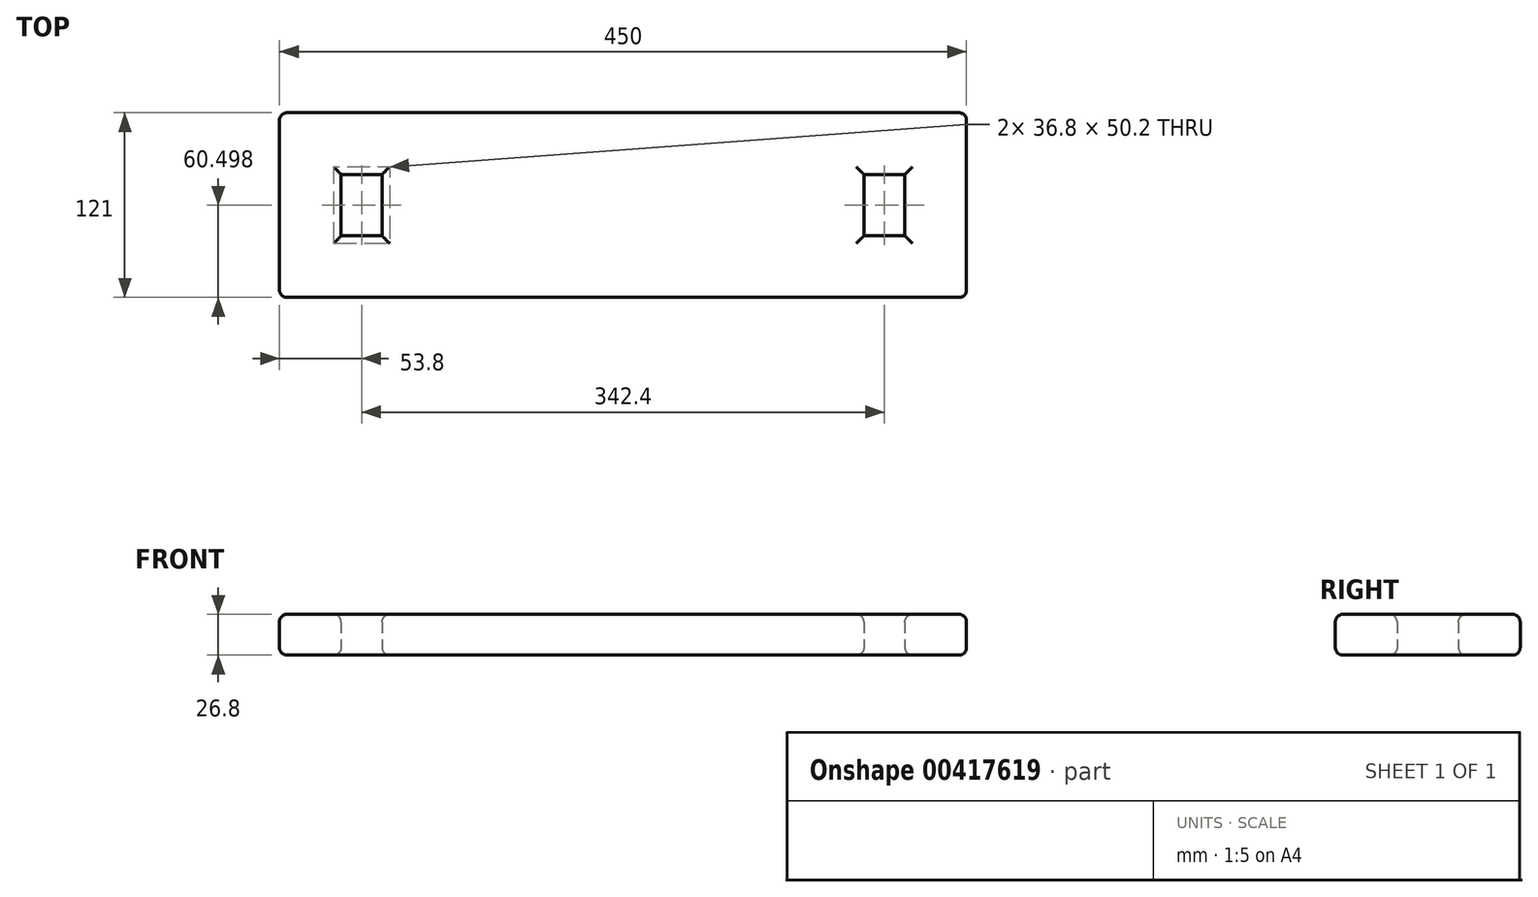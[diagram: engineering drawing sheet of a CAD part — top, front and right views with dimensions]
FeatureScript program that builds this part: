
annotation { "Feature Type Name" : "Feature", "Feature Type Description" : "" }
export const myFeature = defineFeature(function(context is Context, id is Id, definition is map)
    precondition{}
    {
        {
            var Q0;
            Q0=qCreatedBy(makeId("Top.planeOp"),FACE);
            var sketch = newSketch(context, id + "F0", { "sketchPlane" : qUnion([Q0])});
            skLineSegment(sketch, "E0.bottom", {"start": v(-382.8, 117.82) * mm, "end": v(67.2, 117.82) * mm});
            skLineSegment(sketch, "E0.top", {"start": v(-382.8, -3.18) * mm, "end": v(67.2, -3.18) * mm});
            skLineSegment(sketch, "E0.left", {"start": v(-382.8, 117.82) * mm, "end": v(-382.8, -3.18) * mm});
            skLineSegment(sketch, "E0.right", {"start": v(67.2, 117.82) * mm, "end": v(67.2, -3.18) * mm});
            skLineSegment(sketch, "E1.bottom", {"start": v(-342.4, 77.42) * mm, "end": v(-315.6, 77.42) * mm});
            skLineSegment(sketch, "E1.top", {"start": v(-342.4, 37.22) * mm, "end": v(-315.6, 37.22) * mm});
            skLineSegment(sketch, "E1.left", {"start": v(-342.4, 77.42) * mm, "end": v(-342.4, 37.22) * mm});
            skLineSegment(sketch, "E1.right", {"start": v(-315.6, 77.42) * mm, "end": v(-315.6, 37.22) * mm});
            skLineSegment(sketch, "E2.bottom", {"start": v(26.8, 77.42) * mm, "end": v(0, 77.42) * mm});
            skLineSegment(sketch, "E2.top", {"start": v(26.8, 37.22) * mm, "end": v(0, 37.22) * mm});
            skLineSegment(sketch, "E2.left", {"start": v(26.8, 77.42) * mm, "end": v(26.8, 37.22) * mm});
            skLineSegment(sketch, "E2.right", {"start": v(0, 77.42) * mm, "end": v(0, 37.22) * mm});
            skPoint(sketch, "E3.right.end.orphan", {"position": v(-342.4, 37.22) * mm});
            skPoint(sketch, "E4.right.end.orphan", {"position": v(26.8, 37.22) * mm});
            skSolve(sketch);
        }
        {
            var Q0;
            Q0=makeQuery(id+"F0.imprint","IMPRINT",FACE,{"disambiguationData":[TD([[makeQuery(id+"F0.imprint","IMPRINT",EDGE,{"derivedFrom":sQuery(id+"F0.wireOp",EDGE,"E0.bottom")}),-1.0]])]});
            extrude(context, id + "F1", {"entities" : qUnion([Q0]), "depth" : 26.8 * mm});
        }
        {
            var Q0;
            Q0=makeQuery(id+"F1.opExtrude","CAP_FACE",FACE,{"disambiguationData":[OSD([sQuery(id+"F0.wireOp",EDGE,"E0.bottom"),sQuery(id+"F0.wireOp",EDGE,"E0.top"),sQuery(id+"F0.wireOp",EDGE,"E0.left"),sQuery(id+"F0.wireOp",EDGE,"E0.right"),sQuery(id+"F0.wireOp",EDGE,"E1.bottom"),sQuery(id+"F0.wireOp",EDGE,"E1.top"),sQuery(id+"F0.wireOp",EDGE,"E1.left"),sQuery(id+"F0.wireOp",EDGE,"E1.right"),sQuery(id+"F0.wireOp",EDGE,"E2.bottom"),sQuery(id+"F0.wireOp",EDGE,"E2.top"),sQuery(id+"F0.wireOp",EDGE,"E2.left"),sQuery(id+"F0.wireOp",EDGE,"E2.right")])],"isStart":false});
            var Q1;
            Q1=makeQuery(id+"F1.opExtrude","CAP_EDGE",EDGE,{"disambiguationData":[OSD([sQuery(id+"F0.wireOp",EDGE,"E0.top")])],"isStart":false});
            fillet(context, id + "F2", {"entities" : qUnion([Q0, Q1]), "radius" : 5 * mm, "tangentPropagation" : true, "allowEdgeOverflow" : false});
        }
        {
            var Q0;
            Q0=makeQuery(id+"F1.opExtrude","CAP_EDGE",EDGE,{"disambiguationData":[OSD([sQuery(id+"F0.wireOp",EDGE,"E0.top")])],"isStart":true});
            var Q1;
            Q1=makeQuery(id+"F1.opExtrude","CAP_EDGE",EDGE,{"disambiguationData":[OSD([sQuery(id+"F0.wireOp",EDGE,"E0.left")])],"isStart":true});
            var Q2;
            Q2=makeQuery(id+"F1.opExtrude","CAP_EDGE",EDGE,{"disambiguationData":[OSD([sQuery(id+"F0.wireOp",EDGE,"E0.bottom")])],"isStart":true});
            var Q3;
            Q3=makeQuery(id+"F1.opExtrude","CAP_EDGE",EDGE,{"disambiguationData":[OSD([sQuery(id+"F0.wireOp",EDGE,"E0.right")])],"isStart":true});
            var Q4;
            Q4=makeQuery(id+"F1.opExtrude","CAP_EDGE",EDGE,{"disambiguationData":[OSD([sQuery(id+"F0.wireOp",EDGE,"E2.right")])],"isStart":true});
            var Q5;
            Q5=makeQuery(id+"F1.opExtrude","CAP_EDGE",EDGE,{"disambiguationData":[OSD([sQuery(id+"F0.wireOp",EDGE,"E2.left")])],"isStart":true});
            var Q6;
            Q6=makeQuery(id+"F1.opExtrude","CAP_EDGE",EDGE,{"disambiguationData":[OSD([sQuery(id+"F0.wireOp",EDGE,"E2.bottom")])],"isStart":true});
            var Q7;
            Q7=makeQuery(id+"F1.opExtrude","CAP_EDGE",EDGE,{"disambiguationData":[OSD([sQuery(id+"F0.wireOp",EDGE,"E2.top")])],"isStart":true});
            var Q8;
            Q8=makeQuery(id+"F1.opExtrude","CAP_EDGE",EDGE,{"disambiguationData":[OSD([sQuery(id+"F0.wireOp",EDGE,"E1.top")])],"isStart":true});
            var Q9;
            Q9=makeQuery(id+"F1.opExtrude","CAP_EDGE",EDGE,{"disambiguationData":[OSD([sQuery(id+"F0.wireOp",EDGE,"E1.left")])],"isStart":true});
            var Q10;
            Q10=makeQuery(id+"F1.opExtrude","CAP_EDGE",EDGE,{"disambiguationData":[OSD([sQuery(id+"F0.wireOp",EDGE,"E1.right")])],"isStart":true});
            var Q11;
            Q11=makeQuery(id+"F1.opExtrude","CAP_EDGE",EDGE,{"disambiguationData":[OSD([sQuery(id+"F0.wireOp",EDGE,"E1.bottom")])],"isStart":true});
            var Q12;
            Q12=makeQuery(id+"F1.opExtrude","SWEPT_EDGE",EDGE,{"disambiguationData":[OSD([sQuery(id+"F0.wireOp",EDGE,"E0.top"),sQuery(id+"F0.wireOp",EDGE,"E0.left")])]});
            var Q13;
            Q13=makeQuery(id+"F1.opExtrude","SWEPT_EDGE",EDGE,{"disambiguationData":[OSD([sQuery(id+"F0.wireOp",EDGE,"E0.top"),sQuery(id+"F0.wireOp",EDGE,"E0.right")])]});
            var Q14;
            Q14=makeQuery(id+"F1.opExtrude","SWEPT_EDGE",EDGE,{"disambiguationData":[OSD([sQuery(id+"F0.wireOp",EDGE,"E0.bottom"),sQuery(id+"F0.wireOp",EDGE,"E0.left")])]});
            var Q15;
            Q15=makeQuery(id+"F1.opExtrude","SWEPT_EDGE",EDGE,{"disambiguationData":[OSD([sQuery(id+"F0.wireOp",EDGE,"E0.bottom"),sQuery(id+"F0.wireOp",EDGE,"E0.right")])]});
            fillet(context, id + "F3", {"entities" : qUnion([Q0, Q1, Q2, Q3, Q4, Q5, Q6, Q7, Q8, Q9, Q10, Q11, Q12, Q13, Q14, Q15]), "radius" : 5 * mm, "tangentPropagation" : true, "allowEdgeOverflow" : false});
        }
    });
